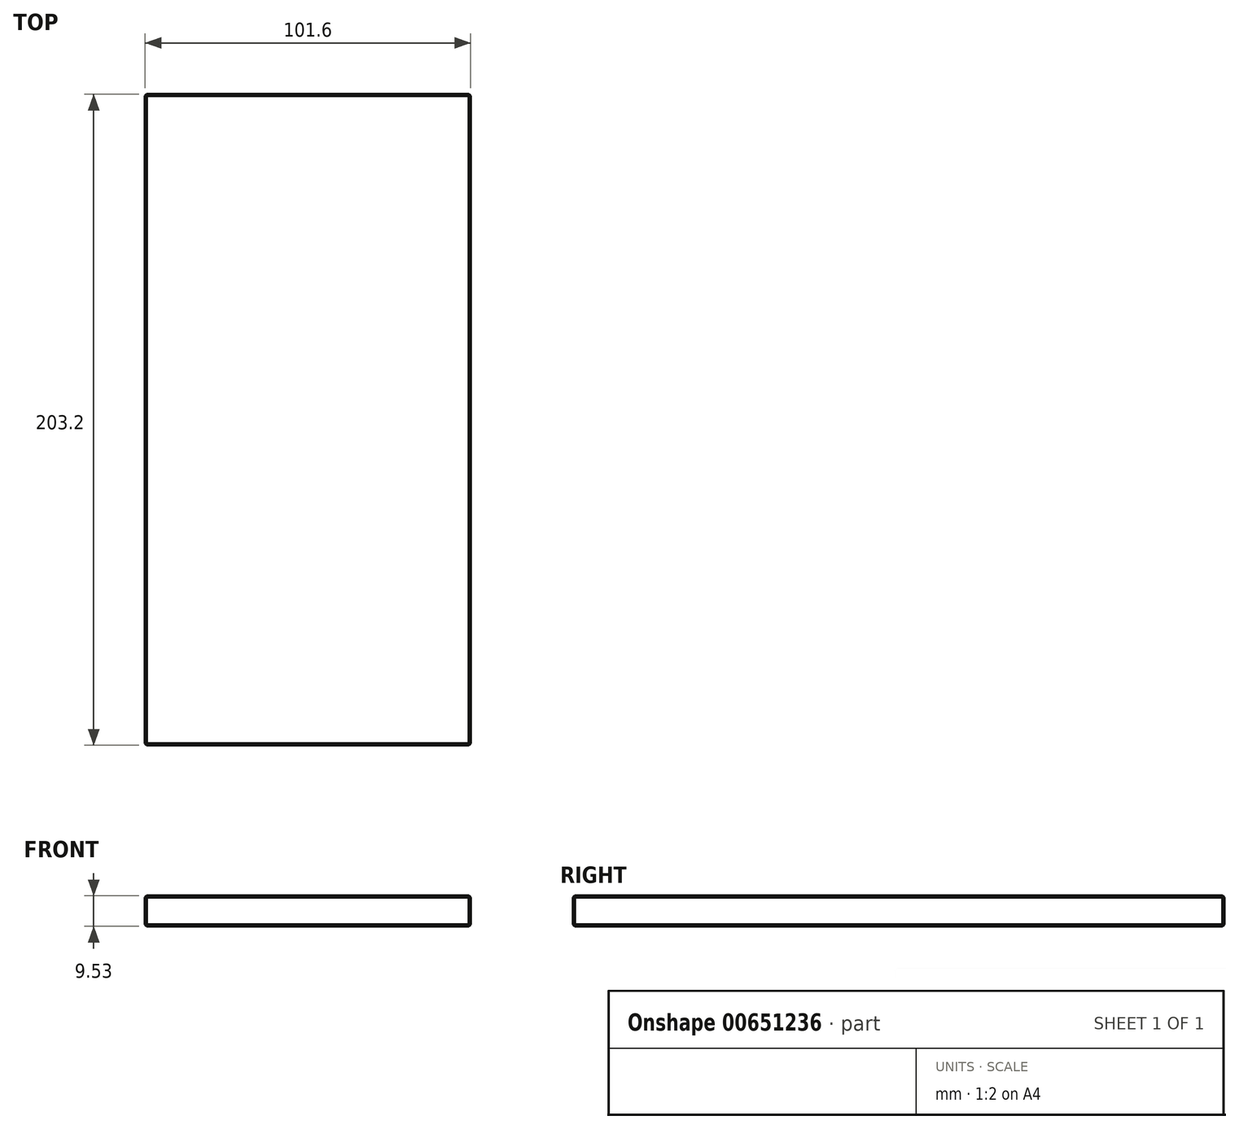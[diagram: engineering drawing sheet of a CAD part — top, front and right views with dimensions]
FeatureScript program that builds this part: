
annotation { "Feature Type Name" : "Feature", "Feature Type Description" : "" }
export const myFeature = defineFeature(function(context is Context, id is Id, definition is map)
    precondition{}
    {
        {
            var Q0;
            Q0=qCreatedBy(makeId("Top.planeOp"),FACE);
            var sketch = newSketch(context, id + "F0", { "sketchPlane" : qUnion([Q0])});
            skLineSegment(sketch, "E0.bottom", {"start": v(50.8, -101.6) * mm, "end": v(-50.8, -101.6) * mm});
            skLineSegment(sketch, "E0.top", {"start": v(50.8, 101.6) * mm, "end": v(-50.8, 101.6) * mm});
            skLineSegment(sketch, "E0.left", {"start": v(50.8, -101.6) * mm, "end": v(50.8, 101.6) * mm});
            skLineSegment(sketch, "E0.right", {"start": v(-50.8, -101.6) * mm, "end": v(-50.8, 101.6) * mm});
            skPoint(sketch, "E0.middle", {"position": v(0, 0) * mm});
            skSolve(sketch);
        }
        {
            var Q0;
            Q0=makeQuery(id+"F0.imprint","IMPRINT",FACE,{"disambiguationData":[TD([[makeQuery(id+"F0.imprint","IMPRINT",EDGE,{"derivedFrom":sQuery(id+"F0.wireOp",EDGE,"E0.bottom")}),-1.0]])]});
            extrude(context, id + "F1", {"entities" : qUnion([Q0]), "depth" : 9.52 * mm, "offsetDistance" : 25.4 * mm});
        }
        {
            var Q0;
            Q0=makeQuery(id+"F1.opExtrude","CAP_FACE",FACE,{"disambiguationData":[OSD([sQuery(id+"F0.wireOp",EDGE,"E0.bottom"),sQuery(id+"F0.wireOp",EDGE,"E0.top"),sQuery(id+"F0.wireOp",EDGE,"E0.left"),sQuery(id+"F0.wireOp",EDGE,"E0.right")])],"isStart":false});
            var Q1;
            Q1=makeQuery(id+"F1.opExtrude","CAP_FACE",FACE,{"disambiguationData":[OSD([sQuery(id+"F0.wireOp",EDGE,"E0.bottom"),sQuery(id+"F0.wireOp",EDGE,"E0.top"),sQuery(id+"F0.wireOp",EDGE,"E0.left"),sQuery(id+"F0.wireOp",EDGE,"E0.right")])],"isStart":true});
            var Q2;
            Q2=makeQuery(id+"F1.opExtrude","SWEPT_FACE",FACE,{"disambiguationData":[OSD([sQuery(id+"F0.wireOp",EDGE,"E0.bottom")])]});
            var Q3;
            Q3=makeQuery(id+"F1.opExtrude","SWEPT_FACE",FACE,{"disambiguationData":[OSD([sQuery(id+"F0.wireOp",EDGE,"E0.left")])]});
            var Q4;
            Q4=makeQuery(id+"F1.opExtrude","SWEPT_FACE",FACE,{"disambiguationData":[OSD([sQuery(id+"F0.wireOp",EDGE,"E0.top")])]});
            chamfer(context, id + "F2", {"entities" : qUnion([Q0, Q1, Q2, Q3, Q4]), "width" : 0.5 * mm, "tangentPropagation" : true});
        }
    });
